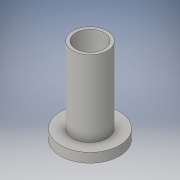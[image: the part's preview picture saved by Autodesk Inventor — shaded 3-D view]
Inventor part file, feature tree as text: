
AUTODESK INVENTOR PART (.ipt)
format: ipt  version: 2016 (Build 200138000, 138)  size: 104,448 bytes
history: native  units: in
note: dims shown in document units (in); Inventor stores cm internally (conversion verified against a paired STEP export)
features: extrude x2, sketch x2
ambient origin geometry x8: Origin, YZ Plane, XZ Plane, XY Plane, X Axis, Y Axis, Z Axis, Center Point
bodies: Solid1 (feature_tree)
feature tree (4):
  extrude  "Extrusion1"  Depth=0.14in
  extrude  "Extrusion2"  Depth=0.374in
  sketch  "Sketch1"  dims[d1=0.29in d4=0.14in]
  sketch  "Sketch2"  dims[d5=0.42in d6=0.0in d7=0.17in d8=0.374in d9=0.0in]
